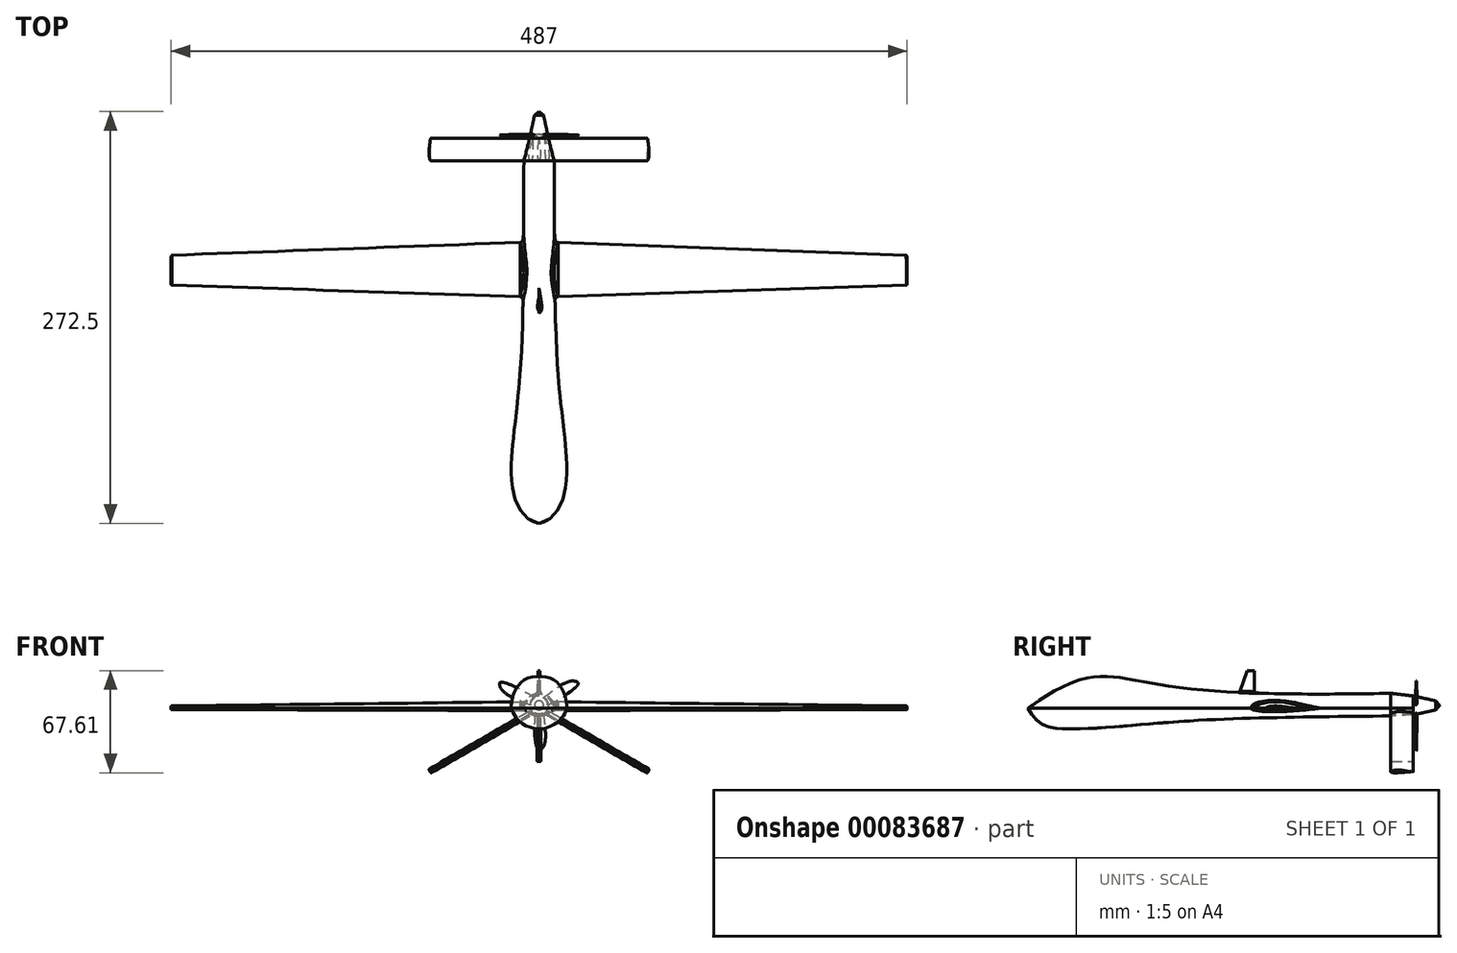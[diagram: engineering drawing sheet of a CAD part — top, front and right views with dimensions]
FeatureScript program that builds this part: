
annotation { "Feature Type Name" : "Feature", "Feature Type Description" : "" }
export const myFeature = defineFeature(function(context is Context, id is Id, definition is map)
    precondition{}
    {
        {
            var Q0;
            Q0=qCreatedBy(makeId("Right.planeOp"),FACE);
            var sketch = newSketch(context, id + "F0", { "sketchPlane" : qUnion([Q0])});
            skLineSegment(sketch, "E0", {"start": v(0, 0) * mm, "end": v(240, 0) * mm});
            skFitSpline(sketch, "E1", {"points": [v(0, 0) * mm, v(37.5, 19.82) * mm, v(94.65, 14.48) * mm, v(240, 10) * mm], "startDerivative": vector(93.49, 65.35) * mm, "endDerivative": vector(326.63, 5.9) * mm});
            skLineSegment(sketch, "E2", {"start": v(240, 10) * mm, "end": v(240, 0) * mm});
            skSolve(sketch);
        }
        {
            var Q0;
            Q0=qCreatedBy(makeId("Front.planeOp"),FACE);
            cPlane(context, id + "F1", {"entities" : qUnion([Q0]), "cplaneType" : CPlaneType.OFFSET, "offset" : 240 * mm, "oppositeDirection" : true, "width" : 150 * mm, "height" : 150 * mm});
        }
        {
            var Q0;
            Q0=qCreatedBy(id+"F1.planeOp",FACE);
            var sketch = newSketch(context, id + "F2", { "sketchPlane" : qUnion([Q0])});
            skArc(sketch, "E3", {"start": v(10, 0) * mm, "mid": v(0, 10) * mm, "end": v(-10, 0) * mm});
            skLineSegment(sketch, "E4", {"start": v(-10, 0) * mm, "end": v(10, 0) * mm});
            skPoint(sketch, "E5.0.start.orphan", {"position": v(0, 10) * mm});
            skSolve(sketch);
        }
        {
            var Q0;
            Q0=qCreatedBy(makeId("Top.planeOp"),FACE);
            var sketch = newSketch(context, id + "F3", { "sketchPlane" : qUnion([Q0])});
            skLineSegment(sketch, "E6", {"start": v(0, 0) * mm, "end": v(0, 272.56) * mm, "construction": true});
            skFitSpline(sketch, "E7.0", {"points": [v(0, 240) * mm, v(-3.33, 240) * mm, v(-6.67, 240) * mm, v(-10, 240) * mm]});
            skFitSpline(sketch, "E8", {"points": [v(-10, 240) * mm, v(-13.37, 88.04) * mm, v(-16.88, 19.92) * mm, v(0, 0) * mm], "startDerivative": vector(-2.86, -342.32) * mm, "endDerivative": vector(133.74, -24.52) * mm});
            skFitSpline(sketch, "E9.MirrorCS", {"points": [v(10, 240) * mm, v(13.37, 88.04) * mm, v(16.88, 19.92) * mm, v(0, 0) * mm], "startDerivative": vector(2.86, -342.32) * mm, "endDerivative": vector(-133.74, -24.52) * mm});
            skSolve(sketch);
        }
        {
            var Q0;
            Q0=qCreatedBy(makeId("Front.planeOp"),FACE);
            cPlane(context, id + "F4", {"entities" : qUnion([Q0]), "cplaneType" : CPlaneType.OFFSET, "offset" : 37.5 * mm, "oppositeDirection" : true, "width" : 150 * mm, "height" : 150 * mm});
        }
        {
            var Q0;
            Q0=qCreatedBy(id+"F4.planeOp",FACE);
            var sketch = newSketch(context, id + "F5", { "sketchPlane" : qUnion([Q0])});
            skArc(sketch, "E10", {"start": v(18.28, 0) * mm, "mid": v(0, 19.82) * mm, "end": v(-18.28, 0) * mm});
            skLineSegment(sketch, "E11", {"start": v(-18.28, 0) * mm, "end": v(18.28, 0) * mm});
            skSolve(sketch);
        }
        {
            var Q0;
            Q0=qCreatedBy(makeId("Front.planeOp"),FACE);
            cPlane(context, id + "F6", {"entities" : qUnion([Q0]), "cplaneType" : CPlaneType.OFFSET, "offset" : 150 * mm, "oppositeDirection" : true, "width" : 150 * mm, "height" : 150 * mm});
        }
        {
            var Q0;
            Q0=qCreatedBy(id+"F6.planeOp",FACE);
            var sketch = newSketch(context, id + "F7", { "sketchPlane" : qUnion([Q0])});
            skArc(sketch, "E12", {"start": v(10.54, 0) * mm, "mid": v(0, 10.12) * mm, "end": v(-10.54, 0) * mm});
            skLineSegment(sketch, "E13", {"start": v(-10.54, 0) * mm, "end": v(10.54, 0) * mm});
            skSolve(sketch);
        }
        {
            var Q0;
            Q0=makeQuery(id+"F2.imprint","IMPRINT",FACE,{"disambiguationData":[TD([[makeQuery(id+"F2.imprint","IMPRINT",EDGE,{"derivedFrom":sQuery(id+"F2.wireOp",EDGE,"E3")}),1.0]])]});
            var Q1;
            Q1=makeQuery(id+"F7.imprint","IMPRINT",FACE,{"disambiguationData":[TD([[makeQuery(id+"F7.imprint","IMPRINT",EDGE,{"derivedFrom":sQuery(id+"F7.wireOp",EDGE,"E12")}),1.0]])]});
            var Q2;
            Q2=makeQuery(id+"F5.imprint","IMPRINT",FACE,{"disambiguationData":[TD([[makeQuery(id+"F5.imprint","IMPRINT",EDGE,{"derivedFrom":sQuery(id+"F5.wireOp",EDGE,"E10")}),1.0]])]});
            var Q3;
            Q3=sQuery(id+"F3.wireOp",VERTEX,"E9.MirrorCS.3.internal");
            var Q4;
            Q4=sQuery(id+"F0.wireOp",EDGE,"E1");
            var Q5;
            Q5=sQuery(id+"F3.wireOp",EDGE,"E9.MirrorCS");
            var Q6;
            Q6=sQuery(id+"F3.wireOp",EDGE,"E8");
            loft(context, id + "F8", {"addGuides" : true, "sheetProfilesArray" : [{ "sheetProfileEntities" : qUnion([Q0]) }, { "sheetProfileEntities" : qUnion([Q1]) }, { "sheetProfileEntities" : qUnion([Q2]) }, { "sheetProfileEntities" : qUnion([Q3]) }], "guidesArray" : [{ "guideEntities" : qUnion([Q4]), "guideDerivativeType" : LoftGuideDerivativeType.DEFAULT, "guideDerivativeMagnitude" : 1 }, { "guideEntities" : qUnion([Q5]), "guideDerivativeType" : LoftGuideDerivativeType.DEFAULT, "guideDerivativeMagnitude" : 1 }, { "guideEntities" : qUnion([Q6]), "guideDerivativeType" : LoftGuideDerivativeType.DEFAULT, "guideDerivativeMagnitude" : 1 }]});
        }
        {
            var Q0;
            Q0=qCreatedBy(makeId("Right.planeOp"),FACE);
            var sketch = newSketch(context, id + "F9", { "sketchPlane" : qUnion([Q0])});
            skPoint(sketch, "E14.0", {"position": v(240, 0) * mm});
            skFitSpline(sketch, "E15", {"points": [v(0, 0) * mm, v(16.5, -12.8) * mm, v(84.8, -9.9) * mm, v(240, -5) * mm], "startDerivative": vector(89.7, -143.98) * mm, "endDerivative": vector(544.57, 5.36) * mm});
            skLineSegment(sketch, "E16", {"start": v(0, 0) * mm, "end": v(240, 0) * mm});
            skSolve(sketch);
        }
        {
            var Q0;
            Q0=qCreatedBy(id+"F1.planeOp",FACE);
            var sketch = newSketch(context, id + "F10", { "sketchPlane" : qUnion([Q0])});
            skFitSpline(sketch, "E17.0", {"points": [v(0, 0) * mm, v(-3.33, 0) * mm, v(-6.67, 0) * mm, v(-10, 0) * mm]});
            skLineSegment(sketch, "E18.0", {"start": v(-10, 0) * mm, "end": v(10, 0) * mm});
            skArc(sketch, "E19", {"start": v(-10, 0) * mm, "mid": v(0, -5) * mm, "end": v(10, 0) * mm});
            skSolve(sketch);
        }
        {
            var Q0;
            Q0=qCreatedBy(id+"F6.planeOp",FACE);
            var sketch = newSketch(context, id + "F11", { "sketchPlane" : qUnion([Q0])});
            skArc(sketch, "E20", {"start": v(-10.54, 0) * mm, "mid": v(0, -6.4) * mm, "end": v(10.54, 0) * mm});
            skLineSegment(sketch, "E21", {"start": v(10.54, 0) * mm, "end": v(-10.54, 0) * mm});
            skSolve(sketch);
        }
        {
            var Q0;
            Q0=qCreatedBy(id+"F4.planeOp",FACE);
            var sketch = newSketch(context, id + "F12", { "sketchPlane" : qUnion([Q0])});
            skArc(sketch, "E22", {"start": v(-18.28, 0) * mm, "mid": v(0, -13.44) * mm, "end": v(18.28, 0) * mm});
            skLineSegment(sketch, "E23", {"start": v(-18.28, 0) * mm, "end": v(18.28, 0) * mm});
            skSolve(sketch);
        }
        {
            var Q1;
            {var subQ0=sQuery(id+"F10.wireOp",EDGE,"E19");Q1=makeQuery(id+"F10.imprint","IMPRINT",FACE,{"disambiguationData":[TD([[makeQuery(id+"F10.imprint","IMPRINT",EDGE,{"derivedFrom":subQ0}),1.0]])]});}
            var Q2;
            Q2=makeQuery(id+"F11.imprint","IMPRINT",FACE,{"disambiguationData":[TD([[makeQuery(id+"F11.imprint","IMPRINT",EDGE,{"derivedFrom":sQuery(id+"F11.wireOp",EDGE,"E20")}),1.0]])]});
            var Q3;
            Q3=makeQuery(id+"F12.imprint","IMPRINT",FACE,{"disambiguationData":[TD([[makeQuery(id+"F12.imprint","IMPRINT",EDGE,{"derivedFrom":sQuery(id+"F12.wireOp",EDGE,"E22")}),1.0]])]});
            var Q4;
            Q4=sQuery(id+"F9.wireOp",VERTEX,"E15.0.internal");
            var Q5;
            Q5=sQuery(id+"F3.wireOp",EDGE,"E8");
            var Q6;
            Q6=sQuery(id+"F3.wireOp",EDGE,"E9.MirrorCS");
            var Q7;
            Q7=sQuery(id+"F9.wireOp",EDGE,"E15");
            loft(context, id + "F13", {"operationType" : NewBodyOperationType.ADD, "addGuides" : true, "sheetProfilesArray" : [{ "sheetProfileEntities" : qUnion([Q1]) }, { "sheetProfileEntities" : qUnion([Q2]) }, { "sheetProfileEntities" : qUnion([Q3]) }, { "sheetProfileEntities" : qUnion([Q4]) }], "guidesArray" : [{ "guideEntities" : qUnion([Q5]), "guideDerivativeType" : LoftGuideDerivativeType.DEFAULT, "guideDerivativeMagnitude" : 1 }, { "guideEntities" : qUnion([Q6]), "guideDerivativeType" : LoftGuideDerivativeType.DEFAULT, "guideDerivativeMagnitude" : 1 }, { "guideEntities" : qUnion([Q7]), "guideDerivativeType" : LoftGuideDerivativeType.DEFAULT, "guideDerivativeMagnitude" : 1 }]});
        }
        {
            var Q0;
            Q0=qCreatedBy(makeId("Right.planeOp"),FACE);
            var sketch = newSketch(context, id + "F14", { "sketchPlane" : qUnion([Q0])});
            skLineSegment(sketch, "E24", {"start": v(0, 0) * mm, "end": v(150, 0) * mm, "construction": true});
            skLineSegment(sketch, "E25", {"start": v(150, 0) * mm, "end": v(186, 0) * mm, "construction": true});
            skFitSpline(sketch, "E26", {"points": [v(150, 0) * mm, v(162.77, 4.35) * mm, v(186, 0) * mm], "startDerivative": vector(1.89, 17.28) * mm, "endDerivative": vector(43.95, -12.7) * mm});
            skFitSpline(sketch, "E27", {"points": [v(150, 0) * mm, v(161.94, -1.41) * mm, v(186, 0) * mm], "startDerivative": vector(11.14, -7.95) * mm, "endDerivative": vector(52.3, 6.57) * mm});
            skSolve(sketch);
        }
        {
            var Q0;
            Q0=qSketchRegion(id+"F14",true);
            extrude(context, id + "F15", {"entities" : qUnion([Q0]), "operationType" : NewBodyOperationType.ADD, "endBound" : BoundingType.SYMMETRIC, "depth" : 25 * mm});
        }
        {
            var Q0;
            Q0=qCreatedBy(makeId("Right.planeOp"),FACE);
            cPlane(context, id + "F16", {"entities" : qUnion([Q0]), "cplaneType" : CPlaneType.OFFSET, "offset" : 243.5 * mm, "width" : 150 * mm, "height" : 150 * mm});
        }
        {
            var Q0;
            Q0=qCreatedBy(id+"F16.planeOp",FACE);
            var sketch = newSketch(context, id + "F17", { "sketchPlane" : qUnion([Q0])});
            skFitSpline(sketch, "E28.0.0", {"points": [v(186, 0) * mm, v(177.65, 2.41) * mm, v(165.41, 6.33) * mm, v(150.27, 2.48) * mm, v(150, 0) * mm]});
            skFitSpline(sketch, "E28.0.1", {"points": [v(150, 0) * mm, v(151.54, -1.1) * mm, v(164.41, -1.68) * mm, v(175.78, -1.28) * mm, v(186, 0) * mm]});
            skLineSegment(sketch, "E29", {"start": v(142.65, 0) * mm, "end": v(197.39, 0) * mm, "construction": true});
            skFitSpline(sketch, "E30", {"points": [v(157.7, 0) * mm, v(162.9, 1.58) * mm, v(177.41, 0) * mm], "startDerivative": vector(0.8, 8.3) * mm, "endDerivative": vector(32.19, -4.29) * mm});
            skFitSpline(sketch, "E31", {"points": [v(157.7, 0) * mm, v(164.23, -0.7) * mm, v(177.41, 0) * mm], "startDerivative": vector(2.27, -4.37) * mm, "endDerivative": vector(24.46, 2.77) * mm});
            skSolve(sketch);
        }
        {
            var Q0;
            Q0=makeQuery(id+"F17.imprint","IMPRINT",FACE,{"disambiguationData":[TD([[makeQuery(id+"F17.imprint","IMPRINT",EDGE,{"derivedFrom":sQuery(id+"F17.wireOp",EDGE,"E30")}),-1.0]])]});
            var Q1;
            Q1=makeQuery(id+"F15.opExtrude","CAP_FACE",FACE,{"disambiguationData":[OSD([sQuery(id+"F14.wireOp",EDGE,"E26"),sQuery(id+"F14.wireOp",EDGE,"E27")])],"isStart":false});
            loft(context, id + "F18", {"sheetProfilesArray" : [{ "sheetProfileEntities" : qUnion([Q0]) }, { "sheetProfileEntities" : qUnion([Q1]) }]});
        }
        {
            var Q0;
            {var subQ0=sQuery(id+"F17.wireOp",EDGE,"E30");var subQ1=sQuery(id+"F17.wireOp",EDGE,"E31");Q0=makeQuery(id+"F18.opLoft","MID_CAP_EDGE",EDGE,{"disambiguationData":[OSD([subQ0,subQ1]),TDD([makeQuery(id+"F17.imprint","INTERSECT",VERTEX,{"disambiguationData":[OD(0.0)],"derivedFrom":[subQ0,subQ1]}),makeQuery(id+"F17.imprint","INTERSECT",VERTEX,{"disambiguationData":[OD(1.0)],"derivedFrom":[subQ0,subQ1]}),makeQuery(id+"F17.imprint","IMPRINT",EDGE,{"derivedFrom":subQ0})])],"capPos":0.0});}
            fillet(context, id + "F19", {"entities" : qUnion([Q0]), "radius" : 0.5 * mm, "tangentPropagation" : true, "allowEdgeOverflow" : false});
        }
        {
            var Q0;
            Q0=makeQuery(id+"F18.opLoft","SWEPT_BODY",BODY,{"disambiguationData":[OSD([sQuery(id+"F14.wireOp",EDGE,"E26"),sQuery(id+"F14.wireOp",EDGE,"E27"),makeQuery(id+"F17.imprint","IMPRINT",FACE,{"disambiguationData":[TD([[makeQuery(id+"F17.imprint","IMPRINT",EDGE,{"derivedFrom":sQuery(id+"F17.wireOp",EDGE,"E30")}),-1.0]])]})])]});
            var Q1;
            Q1=qCreatedBy(makeId("Right.planeOp"),FACE);
            mirror(context, id + "F20", {"operationType" : NewBodyOperationType.ADD, "entities" : qUnion([Q0]), "mirrorPlane" : qUnion([Q1])});
        }
        {
            var Q0;
            Q0=qCreatedBy(makeId("Front.planeOp"),FACE);
            cPlane(context, id + "F21", {"entities" : qUnion([Q0]), "cplaneType" : CPlaneType.OFFSET, "offset" : 255 * mm, "oppositeDirection" : true, "width" : 150 * mm, "height" : 150 * mm});
        }
        {
            var Q0;
            Q0=qCreatedBy(id+"F21.planeOp",FACE);
            var sketch = newSketch(context, id + "F22", { "sketchPlane" : qUnion([Q0])});
            skFitSpline(sketch, "E32.0.0", {"points": [v(0, 10) * mm, v(0.66, 10) * mm, v(1.3, 9.94) * mm, v(1.95, 9.8) * mm, v(2.6, 9.68) * mm, v(3.22, 9.5) * mm, v(3.83, 9.24) * mm, v(4.43, 8.99) * mm, v(5, 8.68) * mm, v(5.56, 8.31) * mm, v(6.1, 7.95) * mm, v(6.6, 7.54) * mm, v(7.07, 7.07) * mm, v(7.53, 6.6) * mm, v(7.95, 6.1) * mm, v(8.31, 5.56) * mm, v(8.68, 5.01) * mm, v(8.99, 4.43) * mm, v(9.24, 3.83) * mm, v(9.49, 3.22) * mm, v(9.68, 2.6) * mm, v(9.8, 1.95) * mm, v(9.94, 1.3) * mm, v(10, 0.66) * mm, v(10, 0) * mm]});
            skFitSpline(sketch, "E32.0.1", {"points": [v(10, 0) * mm, v(9.42, -0.78) * mm, v(8.75, -1.47) * mm, v(8, -2.1) * mm, v(7.27, -2.72) * mm, v(6.46, -3.25) * mm, v(5.6, -3.68) * mm, v(4.72, -4.11) * mm, v(3.82, -4.44) * mm, v(2.87, -4.67) * mm, v(1.93, -4.89) * mm, v(0.97, -5) * mm, v(0, -5) * mm]});
            skFitSpline(sketch, "E32.0.2", {"points": [v(0, -5) * mm, v(-0.97, -5) * mm, v(-1.93, -4.89) * mm, v(-2.87, -4.67) * mm, v(-3.82, -4.44) * mm, v(-4.72, -4.11) * mm, v(-5.6, -3.68) * mm, v(-6.46, -3.25) * mm, v(-7.26, -2.72) * mm, v(-8, -2.1) * mm, v(-8.75, -1.48) * mm, v(-9.42, -0.78) * mm, v(-10, 0) * mm]});
            skFitSpline(sketch, "E32.0.3", {"points": [v(-10, 0) * mm, v(-10, 0.66) * mm, v(-9.94, 1.3) * mm, v(-9.8, 1.95) * mm, v(-9.68, 2.6) * mm, v(-9.5, 3.22) * mm, v(-9.24, 3.83) * mm, v(-8.99, 4.43) * mm, v(-8.68, 5) * mm, v(-8.31, 5.56) * mm, v(-7.95, 6.1) * mm, v(-7.54, 6.6) * mm, v(-7.07, 7.07) * mm, v(-6.6, 7.53) * mm, v(-6.1, 7.95) * mm, v(-5.56, 8.31) * mm, v(-5.01, 8.68) * mm, v(-4.43, 8.99) * mm, v(-3.83, 9.24) * mm, v(-3.22, 9.49) * mm, v(-2.6, 9.68) * mm, v(-1.95, 9.8) * mm, v(-1.3, 9.94) * mm, v(-0.66, 10) * mm, v(0, 10) * mm]});
            skCircle(sketch, "E33", {"center": v(0, 2) * mm, "radius": 6.25 * mm});
            skLineSegment(sketch, "E34", {"start": v(10, 0) * mm, "end": v(-10, 0) * mm, "construction": true});
            skPoint(sketch, "E35", {"position": v(5.92, 0) * mm});
            skPoint(sketch, "E36", {"position": v(-5.92, 0) * mm});
            skPoint(sketch, "E37", {"position": v(0, 8.25) * mm});
            skPoint(sketch, "E38", {"position": v(0, -4.25) * mm});
            skSolve(sketch);
        }
        {
            var Q0;
            Q0=qCreatedBy(makeId("Front.planeOp"),FACE);
            cPlane(context, id + "F23", {"entities" : qUnion([Q0]), "cplaneType" : CPlaneType.OFFSET, "offset" : 270 * mm, "oppositeDirection" : true, "width" : 150 * mm, "height" : 150 * mm});
        }
        {
            var Q0;
            Q0=qCreatedBy(makeId("Top.planeOp"),FACE);
            var sketch = newSketch(context, id + "F24", { "sketchPlane" : qUnion([Q0])});
            skPoint(sketch, "E39.0", {"position": v(-10, 240) * mm});
            skPoint(sketch, "E40.0", {"position": v(10, 240) * mm});
            skPoint(sketch, "E41.0", {"position": v(-5.92, 255) * mm});
            skPoint(sketch, "E42.0", {"position": v(5.92, 255) * mm});
            skLineSegment(sketch, "E43", {"start": v(10, 240) * mm, "end": v(5.92, 255) * mm});
            skLineSegment(sketch, "E44", {"start": v(-10, 240) * mm, "end": v(-5.92, 255) * mm});
            skSolve(sketch);
        }
        {
            var Q1;
            {var subQ0=sQuery(id+"F10.wireOp",EDGE,"E19");Q1=makeQuery(id+"F13.boolean.opBoolean","MERGE",FACE,{"derivedFrom":[makeQuery(id+"F8.opLoft","CAP_FACE",FACE,{"disambiguationData":[OSD([makeQuery(id+"F2.imprint","IMPRINT",FACE,{"disambiguationData":[TD([[makeQuery(id+"F2.imprint","IMPRINT",EDGE,{"derivedFrom":sQuery(id+"F2.wireOp",EDGE,"E3")}),1.0]])]})])],"isStart":true}),makeQuery(id+"F13.opLoft","CAP_FACE",FACE,{"disambiguationData":[OSD([makeQuery(id+"F10.imprint","IMPRINT",FACE,{"disambiguationData":[TD([[makeQuery(id+"F10.imprint","IMPRINT",EDGE,{"derivedFrom":subQ0}),1.0]])]})])],"isStart":true})]});}
            var Q2;
            Q2=makeQuery(id+"F22.imprint","IMPRINT",FACE,{"disambiguationData":[TD([[makeQuery(id+"F22.imprint","IMPRINT",EDGE,{"derivedFrom":sQuery(id+"F22.wireOp",EDGE,"E33")}),1.0]])]});
            var Q3;
            Q3=sQuery(id+"F24.wireOp",EDGE,"E44");
            var Q4;
            Q4=sQuery(id+"F24.wireOp",EDGE,"E43");
            loft(context, id + "F25", {"operationType" : NewBodyOperationType.ADD, "addGuides" : true, "sheetProfilesArray" : [{ "sheetProfileEntities" : qUnion([Q1]) }, { "sheetProfileEntities" : qUnion([Q2]) }], "guidesArray" : [{ "guideEntities" : qUnion([Q3]), "guideDerivativeType" : LoftGuideDerivativeType.DEFAULT, "guideDerivativeMagnitude" : 1 }, { "guideEntities" : qUnion([Q4]), "guideDerivativeType" : LoftGuideDerivativeType.DEFAULT, "guideDerivativeMagnitude" : 1 }]});
        }
        {
            var Q0;
            Q0=qCreatedBy(id+"F23.planeOp",FACE);
            var sketch = newSketch(context, id + "F26", { "sketchPlane" : qUnion([Q0])});
            skCircle(sketch, "E45", {"center": v(0, 2) * mm, "radius": 3 * mm});
            skSolve(sketch);
        }
        {
            var Q1;
            Q1=makeQuery(id+"F25.opLoft","CAP_FACE",FACE,{"disambiguationData":[OSD([makeQuery(id+"F22.imprint","IMPRINT",FACE,{"disambiguationData":[TD([[makeQuery(id+"F22.imprint","IMPRINT",EDGE,{"derivedFrom":sQuery(id+"F22.wireOp",EDGE,"E33")}),1.0]])]})])],"isStart":true});
            var Q2;
            Q2=makeQuery(id+"F26.imprint","IMPRINT",FACE,{"disambiguationData":[TD([[makeQuery(id+"F26.imprint","IMPRINT",EDGE,{"derivedFrom":sQuery(id+"F26.wireOp",EDGE,"E45")}),1.0]])]});
            loft(context, id + "F27", {"operationType" : NewBodyOperationType.ADD, "sheetProfilesArray" : [{ "sheetProfileEntities" : qUnion([Q1]) }, { "sheetProfileEntities" : qUnion([Q2]) }]});
        }
        {
            var Q0;
            Q0=qCreatedBy(makeId("Front.planeOp"),FACE);
            cPlane(context, id + "F28", {"entities" : qUnion([Q0]), "cplaneType" : CPlaneType.OFFSET, "offset" : 272.5 * mm, "oppositeDirection" : true, "width" : 150 * mm, "height" : 150 * mm});
        }
        {
            var Q0;
            Q0=qCreatedBy(id+"F28.planeOp",FACE);
            var sketch = newSketch(context, id + "F29", { "sketchPlane" : qUnion([Q0])});
            skFitSpline(sketch, "E46.0.0", {"points": [v(3, 2) * mm, v(3, 1.6) * mm, v(2.92, 1.22) * mm, v(2.77, 0.85) * mm, v(2.62, 0.49) * mm, v(2.4, 0.16) * mm, v(2.12, -0.12) * mm, v(1.84, -0.4) * mm, v(1.52, -0.62) * mm, v(1.15, -0.77) * mm, v(0.78, -0.92) * mm, v(0.4, -1) * mm, v(0, -1) * mm]});
            skFitSpline(sketch, "E46.0.1", {"points": [v(0, -1) * mm, v(-0.4, -1) * mm, v(-0.78, -0.92) * mm, v(-1.15, -0.77) * mm, v(-1.51, -0.62) * mm, v(-1.84, -0.4) * mm, v(-2.12, -0.12) * mm, v(-2.4, 0.16) * mm, v(-2.62, 0.48) * mm, v(-2.77, 0.85) * mm, v(-2.92, 1.22) * mm, v(-3, 1.6) * mm, v(-3, 2) * mm]});
            skFitSpline(sketch, "E46.0.2", {"points": [v(-3, 2) * mm, v(-3, 2.4) * mm, v(-2.92, 2.78) * mm, v(-2.77, 3.15) * mm, v(-2.62, 3.51) * mm, v(-2.4, 3.84) * mm, v(-2.12, 4.12) * mm, v(-1.84, 4.4) * mm, v(-1.52, 4.62) * mm, v(-1.15, 4.77) * mm, v(-0.78, 4.92) * mm, v(-0.4, 5) * mm, v(0, 5) * mm]});
            skFitSpline(sketch, "E46.0.3", {"points": [v(0, 5) * mm, v(0.4, 5) * mm, v(0.78, 4.92) * mm, v(1.15, 4.77) * mm, v(1.51, 4.62) * mm, v(1.84, 4.4) * mm, v(2.12, 4.12) * mm, v(2.4, 3.84) * mm, v(2.62, 3.52) * mm, v(2.77, 3.15) * mm, v(2.92, 2.78) * mm, v(3, 2.4) * mm, v(3, 2) * mm]});
            skPoint(sketch, "E47", {"position": v(0, 2) * mm});
            skSolve(sketch);
        }
        {
            var Q1;
            Q1=makeQuery(id+"F27.opLoft","CAP_FACE",FACE,{"disambiguationData":[OSD([makeQuery(id+"F26.imprint","IMPRINT",FACE,{"disambiguationData":[TD([[makeQuery(id+"F26.imprint","IMPRINT",EDGE,{"derivedFrom":sQuery(id+"F26.wireOp",EDGE,"E45")}),1.0]])]})])],"isStart":true});
            var Q2;
            Q2=sQuery(id+"F29.wireOp",VERTEX,"E47");
            loft(context, id + "F30", {"operationType" : NewBodyOperationType.ADD, "sheetProfilesArray" : [{ "sheetProfileEntities" : qUnion([Q1]) }, { "sheetProfileEntities" : qUnion([Q2]) }]});
        }
        {
            var Q0;
            Q0=qCreatedBy(makeId("Right.planeOp"),FACE);
            cPlane(context, id + "F31", {"entities" : qUnion([Q0]), "cplaneType" : CPlaneType.OFFSET, "offset" : 72 * mm, "width" : 150 * mm, "height" : 150 * mm});
        }
        {
            var Q0;
            Q0=qCreatedBy(id+"F31.planeOp",FACE);
            var sketch = newSketch(context, id + "F32", { "sketchPlane" : qUnion([Q0])});
            skLineSegment(sketch, "E48", {"start": v(0, 0) * mm, "end": v(0, -42) * mm, "construction": true});
            skLineSegment(sketch, "E49", {"start": v(0, -42) * mm, "end": v(271.23, -42) * mm});
            skSolve(sketch);
        }
        {
            assignVariable(context, id + "F33", {"name" : "angle", "anyValue" : 120});
        }
        {
            var Q0;
            Q0=sQuery(id+"F32.wireOp",EDGE,"E49");
            cPlane(context, id + "F34", {"entities" : qUnion([Q0]), "cplaneType" : CPlaneType.LINE_ANGLE, "offset" : 150 * mm, "angle" : (getVariable(context, 'angle')) * degree, "width" : 150 * mm, "height" : 150 * mm});
        }
        {
            var Q0;
            Q0=qCreatedBy(id+"F34.planeOp",FACE);
            var sketch = newSketch(context, id + "F35", { "sketchPlane" : qUnion([Q0])});
            skFitSpline(sketch, "E50.0", {"points": [v(240, 5) * mm, v(245, 4.32) * mm, v(250, 3.64) * mm, v(255, 2.96) * mm], "construction": true});
            skLineSegment(sketch, "E51.0", {"start": v(0, -0.37) * mm, "end": v(242.6, -0.37) * mm, "construction": true});
            skPoint(sketch, "E52.orphan", {"position": v(271.23, -0.37) * mm});
            skFitSpline(sketch, "E53", {"points": [v(240, -0.37) * mm, v(244.56, 1.55) * mm, v(255, -0.37) * mm], "startDerivative": vector(6.04, 10.7) * mm, "endDerivative": vector(29.02, -7.53) * mm});
            skFitSpline(sketch, "E54", {"points": [v(240, -0.37) * mm, v(244.42, -1.27) * mm, v(255, -0.37) * mm], "startDerivative": vector(3.63, -7.22) * mm, "endDerivative": vector(30.34, 2.29) * mm});
            skSolve(sketch);
        }
        {
            var Q0;
            Q0=makeQuery(id+"F35.imprint","IMPRINT",FACE,{"disambiguationData":[TD([[makeQuery(id+"F35.imprint","IMPRINT",EDGE,{"derivedFrom":sQuery(id+"F35.wireOp",EDGE,"E53")}),-1.0]])]});
            extrude(context, id + "F36", {"entities" : qUnion([Q0]), "oppositeDirection" : true, "depth" : 80 * mm});
        }
        {
            var Q0;
            Q0=makeQuery(id+"F36.opExtrude","CAP_EDGE",EDGE,{"disambiguationData":[OSD([sQuery(id+"F35.wireOp",EDGE,"E53")])],"isStart":true});
            var Q1;
            Q1=makeQuery(id+"F36.opExtrude","CAP_EDGE",EDGE,{"disambiguationData":[OSD([sQuery(id+"F35.wireOp",EDGE,"E54")])],"isStart":true});
            fillet(context, id + "F37", {"entities" : qUnion([Q0, Q1]), "radius" : 0.5 * mm, "tangentPropagation" : true, "allowEdgeOverflow" : false});
        }
        {
            var Q0;
            Q0=makeQuery(id+"F36.opExtrude","SWEPT_BODY",BODY,{"disambiguationData":[OSD([sQuery(id+"F35.wireOp",EDGE,"E53"),sQuery(id+"F35.wireOp",EDGE,"E54")])]});
            var Q1;
            Q1=qCreatedBy(makeId("Right.planeOp"),FACE);
            mirror(context, id + "F38", {"operationType" : NewBodyOperationType.ADD, "entities" : qUnion([Q0]), "mirrorPlane" : qUnion([Q1])});
        }
        {
            var Q0;
            Q0=qCreatedBy(makeId("Top.planeOp"),FACE);
            var sketch = newSketch(context, id + "F39", { "sketchPlane" : qUnion([Q0])});
            skLineSegment(sketch, "E55", {"start": v(0, 0) * mm, "end": v(0, 257) * mm, "construction": true});
            skEllipse(sketch, "E56", {"center": v(0, 257) * mm, "majorRadius": 2.5 * mm, "minorRadius": 0.6 * mm, "majorAxis": v(-1, 0)});
            skSolve(sketch);
        }
        {
            var Q0;
            Q0=qCreatedBy(makeId("Front.planeOp"),FACE);
            cPlane(context, id + "F40", {"entities" : qUnion([Q0]), "cplaneType" : CPlaneType.OFFSET, "offset" : 257 * mm, "oppositeDirection" : true, "width" : 150 * mm, "height" : 150 * mm});
        }
        {
            var Q0;
            Q0=qCreatedBy(id+"F40.planeOp",FACE);
            var sketch = newSketch(context, id + "F41", { "sketchPlane" : qUnion([Q0])});
            skLineSegment(sketch, "E57.0", {"start": v(2.5, 0) * mm, "end": v(-2.5, 0) * mm});
            skLineSegment(sketch, "E58", {"start": v(0, 0) * mm, "end": v(0, -28) * mm, "construction": true});
            skFitSpline(sketch, "E59", {"points": [v(2.5, 0) * mm, v(4.19, -20.46) * mm, v(0, -28) * mm], "startDerivative": vector(5.82, -52.04) * mm, "endDerivative": vector(-22.98, -9.89) * mm});
            skFitSpline(sketch, "E60", {"points": [v(-2.5, 0) * mm, v(-2.5, -20.53) * mm, v(0, -28) * mm], "startDerivative": vector(-3.63, -41.05) * mm, "endDerivative": vector(9.75, -1.43) * mm});
            skSolve(sketch);
        }
        {
            var Q1;
            Q1=makeQuery(id+"F39.imprint","IMPRINT",FACE,{"disambiguationData":[TD([[makeQuery(id+"F39.imprint","IMPRINT",EDGE,{"derivedFrom":sQuery(id+"F39.wireOp",EDGE,"E56")}),1.0]])]});
            var Q2;
            Q2=sQuery(id+"F41.wireOp",VERTEX,"E60.end");
            var Q3;
            Q3=sQuery(id+"F41.wireOp",EDGE,"E59");
            var Q4;
            Q4=sQuery(id+"F41.wireOp",EDGE,"E60");
            loft(context, id + "F42", {"addGuides" : true, "sheetProfilesArray" : [{ "sheetProfileEntities" : qUnion([Q1]) }, { "sheetProfileEntities" : qUnion([Q2]) }], "guidesArray" : [{ "guideEntities" : qUnion([Q3]), "guideDerivativeType" : LoftGuideDerivativeType.DEFAULT, "guideDerivativeMagnitude" : 1 }, { "guideEntities" : qUnion([Q4]), "guideDerivativeType" : LoftGuideDerivativeType.DEFAULT, "guideDerivativeMagnitude" : 1 }]});
        }
        {
            var Q0;
            Q0=qCreatedBy(makeId("Top.planeOp"),FACE);
            cPlane(context, id + "F43", {"entities" : qUnion([Q0]), "cplaneType" : CPlaneType.OFFSET, "offset" : 2 * mm, "width" : 150 * mm, "height" : 150 * mm});
        }
        {
            var Q0;
            Q0=qCreatedBy(id+"F43.planeOp",FACE);
            var sketch = newSketch(context, id + "F44", { "sketchPlane" : qUnion([Q0])});
            skLineSegment(sketch, "E61", {"start": v(0, 0) * mm, "end": v(0, 416.26) * mm, "construction": true});
            skSolve(sketch);
        }
        {
            var Q0;
            Q0=makeQuery(id+"F42.opLoft","SWEPT_BODY",BODY,{"disambiguationData":[OSD([makeQuery(id+"F39.imprint","IMPRINT",FACE,{"disambiguationData":[TD([[makeQuery(id+"F39.imprint","IMPRINT",EDGE,{"derivedFrom":sQuery(id+"F39.wireOp",EDGE,"E56")}),1.0]])]}),sQuery(id+"F41.wireOp",VERTEX,"E60.end"),sQuery(id+"F41.wireOp",EDGE,"E59"),sQuery(id+"F41.wireOp",EDGE,"E60")])]});
            var Q1;
            Q1=sQuery(id+"F44.wireOp",EDGE,"E61");
            circularPattern(context, id + "F45", {"operationType" : NewBodyOperationType.ADD, "entities" : qUnion([Q0]), "axis" : qUnion([Q1]), "angle" : 120 * degree, "instanceCount" : 3});
        }
        {
            var Q0;
            Q0=makeQuery(id+"F15.boolean.opBoolean","INTERSECT",EDGE,{"disambiguationData":[OD(1.0)],"derivedFrom":[makeQuery(id+"F13.opLoft","SWEPT_FACE",FACE,{"disambiguationData":[OSD([sQuery(id+"F3.wireOp",EDGE,"E8"),sQuery(id+"F9.wireOp",EDGE,"E15"),sQuery(id+"F10.wireOp",EDGE,"E19"),sQuery(id+"F11.wireOp",EDGE,"E20"),sQuery(id+"F12.wireOp",EDGE,"E22")])]}),makeQuery(id+"F15.opExtrude","SWEPT_FACE",FACE,{"disambiguationData":[OSD([sQuery(id+"F14.wireOp",EDGE,"E27")])]})]});
            var Q1;
            Q1=makeQuery(id+"F15.boolean.opBoolean","INTERSECT",EDGE,{"disambiguationData":[OD(0.0)],"derivedFrom":[makeQuery(id+"F13.opLoft","SWEPT_FACE",FACE,{"disambiguationData":[OSD([sQuery(id+"F3.wireOp",EDGE,"E8"),sQuery(id+"F9.wireOp",EDGE,"E15"),sQuery(id+"F10.wireOp",EDGE,"E19"),sQuery(id+"F11.wireOp",EDGE,"E20"),sQuery(id+"F12.wireOp",EDGE,"E22")])]}),makeQuery(id+"F15.opExtrude","SWEPT_FACE",FACE,{"disambiguationData":[OSD([sQuery(id+"F14.wireOp",EDGE,"E27")])]})]});
            var Q2;
            Q2=makeQuery(id+"F15.boolean.opBoolean","INTERSECT",EDGE,{"disambiguationData":[OD(1.0)],"derivedFrom":[makeQuery(id+"F8.opLoft","SWEPT_FACE",FACE,{"disambiguationData":[OSD([sQuery(id+"F0.wireOp",EDGE,"E1"),sQuery(id+"F2.wireOp",EDGE,"E3"),sQuery(id+"F3.wireOp",EDGE,"E9.MirrorCS"),sQuery(id+"F5.wireOp",EDGE,"E10"),sQuery(id+"F7.wireOp",EDGE,"E12")])]}),makeQuery(id+"F15.opExtrude","SWEPT_FACE",FACE,{"disambiguationData":[OSD([sQuery(id+"F14.wireOp",EDGE,"E26")])]})]});
            var Q3;
            Q3=makeQuery(id+"F15.boolean.opBoolean","INTERSECT",EDGE,{"disambiguationData":[OD(0.0)],"derivedFrom":[makeQuery(id+"F8.opLoft","SWEPT_FACE",FACE,{"disambiguationData":[OSD([sQuery(id+"F0.wireOp",EDGE,"E1"),sQuery(id+"F2.wireOp",EDGE,"E3"),sQuery(id+"F3.wireOp",EDGE,"E9.MirrorCS"),sQuery(id+"F5.wireOp",EDGE,"E10"),sQuery(id+"F7.wireOp",EDGE,"E12")])]}),makeQuery(id+"F15.opExtrude","SWEPT_FACE",FACE,{"disambiguationData":[OSD([sQuery(id+"F14.wireOp",EDGE,"E26")])]})]});
            fillet(context, id + "F46", {"entities" : qUnion([Q0, Q1, Q2, Q3]), "radius" : 2.5 * mm, "tangentPropagation" : true, "allowEdgeOverflow" : false});
        }
        {
            var Q0;
            Q0=qCreatedBy(makeId("Top.planeOp"),FACE);
            cPlane(context, id + "F47", {"entities" : qUnion([Q0]), "cplaneType" : CPlaneType.OFFSET, "offset" : 35 * mm, "oppositeDirection" : true, "width" : 150 * mm, "height" : 150 * mm});
        }
        {
            var Q0;
            Q0=qCreatedBy(id+"F47.planeOp",FACE);
            var sketch = newSketch(context, id + "F48", { "sketchPlane" : qUnion([Q0])});
            skLineSegment(sketch, "E62", {"start": v(0, 0) * mm, "end": v(0, 240) * mm, "construction": true});
            skFitSpline(sketch, "E63", {"points": [v(0, 240) * mm, v(-1.2, 243.6) * mm, v(0, 255) * mm], "startDerivative": vector(-6.2, 2.4) * mm, "endDerivative": vector(4.32, 22.5) * mm});
            skFitSpline(sketch, "E64.MirrorCS", {"points": [v(0, 240) * mm, v(1.2, 243.6) * mm, v(0, 255) * mm], "startDerivative": vector(6.2, 2.4) * mm, "endDerivative": vector(-4.32, 22.5) * mm});
            skSolve(sketch);
        }
        {
            var Q0;
            Q0=makeQuery(id+"F48.imprint","IMPRINT",FACE,{"disambiguationData":[TD([[makeQuery(id+"F48.imprint","IMPRINT",EDGE,{"derivedFrom":sQuery(id+"F48.wireOp",EDGE,"E63")}),-1.0]])]});
            var Q1;
            {var subQ0=makeQuery(id+"F36.opExtrude","SWEPT_FACE",FACE,{"disambiguationData":[OSD([sQuery(id+"F35.wireOp",EDGE,"E53")])]});var subQ1=sQuery(id+"F24.wireOp",EDGE,"E43");var subQ2=sQuery(id+"F22.wireOp",EDGE,"E33");var subQ3=sQuery(id+"F10.wireOp",EDGE,"E19");var subQ4=sQuery(id+"F9.wireOp",EDGE,"E15");var subQ5=makeQuery(id+"F25.opLoft","SWEPT_FACE",FACE,{"disambiguationData":[OSD([sQuery(id+"F3.wireOp",EDGE,"E9.MirrorCS"),subQ4,subQ3,subQ2,subQ1])]});var subQ6=makeQuery(id+"F36.opExtrude","SWEPT_FACE",FACE,{"disambiguationData":[OSD([sQuery(id+"F35.wireOp",EDGE,"E54")])]});Q1=makeQuery(id+"F38.boolean.opBoolean","SPLIT",FACE,{"disambiguationData":[TD([makeQuery(id+"F13.opLoft","SWEPT_FACE",FACE,{"disambiguationData":[OSD([sQuery(id+"F3.wireOp",EDGE,"E8"),subQ4,subQ3,sQuery(id+"F11.wireOp",EDGE,"E20"),sQuery(id+"F12.wireOp",EDGE,"E22")])]}),subQ5,makeQuery(id+"F27.opLoft","SWEPT_FACE",FACE,{"disambiguationData":[OSD([subQ2,subQ1,sQuery(id+"F24.wireOp",EDGE,"E44"),sQuery(id+"F26.wireOp",EDGE,"E45")])]}),subQ0,subQ6,makeQuery(id+"F38.opPattern","COPY",FACE,{"derivedFrom":subQ0,"instanceName":"1"}),makeQuery(id+"F38.opPattern","COPY",FACE,{"derivedFrom":subQ6,"instanceName":"1"})])],"derivedFrom":subQ5});}
            extrude(context, id + "F49", {"entities" : qUnion([Q0]), "operationType" : NewBodyOperationType.ADD, "endBound" : BoundingType.UP_TO_SURFACE, "endBoundEntityFace" : qUnion([Q1]), "depth" : 25 * mm});
        }
        {
            var Q0;
            Q0=qCreatedBy(makeId("Top.planeOp"),FACE);
            cPlane(context, id + "F50", {"entities" : qUnion([Q0]), "cplaneType" : CPlaneType.OFFSET, "offset" : 25 * mm, "width" : 150 * mm, "height" : 150 * mm});
        }
        {
            var Q0;
            Q0=qCreatedBy(id+"F50.planeOp",FACE);
            var sketch = newSketch(context, id + "F51", { "sketchPlane" : qUnion([Q0])});
            skLineSegment(sketch, "E65", {"start": v(0, 0) * mm, "end": v(0, 145) * mm, "construction": true});
            skFitSpline(sketch, "E66", {"points": [v(0, 145) * mm, v(-0.66, 146.79) * mm, v(0, 150) * mm], "startDerivative": vector(-4.26, 2.06) * mm, "endDerivative": vector(2.38, 11.26) * mm});
            skFitSpline(sketch, "E67.MirrorCS", {"points": [v(0, 145) * mm, v(0.66, 146.79) * mm, v(0, 150) * mm], "startDerivative": vector(4.26, 2.06) * mm, "endDerivative": vector(-2.38, 11.26) * mm});
            skSolve(sketch);
        }
        {
            var Q0;
            Q0=qCreatedBy(makeId("Top.planeOp"),FACE);
            cPlane(context, id + "F52", {"entities" : qUnion([Q0]), "cplaneType" : CPlaneType.OFFSET, "offset" : 10 * mm, "width" : 150 * mm, "height" : 150 * mm});
        }
        {
            var Q0;
            Q0=qCreatedBy(id+"F52.planeOp",FACE);
            var sketch = newSketch(context, id + "F53", { "sketchPlane" : qUnion([Q0])});
            skLineSegment(sketch, "E68", {"start": v(0, 0) * mm, "end": v(0, 140) * mm, "construction": true});
            skPoint(sketch, "E69.0", {"position": v(0, 150) * mm});
            skFitSpline(sketch, "E70", {"points": [v(0, 140) * mm, v(-0.92, 142) * mm, v(0, 150) * mm], "startDerivative": vector(-6.44, 5.81) * mm, "endDerivative": vector(4.8, 27.45) * mm});
            skFitSpline(sketch, "E71.MirrorCS", {"points": [v(0, 140) * mm, v(0.92, 142) * mm, v(0, 150) * mm], "startDerivative": vector(6.44, 5.81) * mm, "endDerivative": vector(-4.8, 27.45) * mm});
            skSolve(sketch);
        }
        {
            var Q1;
            Q1=makeQuery(id+"F51.imprint","IMPRINT",FACE,{"disambiguationData":[TD([[makeQuery(id+"F51.imprint","IMPRINT",EDGE,{"derivedFrom":sQuery(id+"F51.wireOp",EDGE,"E66")}),-1.0]])]});
            var Q2;
            Q2=qSketchRegion(id+"F53",true);
            loft(context, id + "F54", {"operationType" : NewBodyOperationType.ADD, "sheetProfilesArray" : [{ "sheetProfileEntities" : qUnion([Q1]) }, { "sheetProfileEntities" : qUnion([Q2]) }]});
        }
        {
            var Q0;
            {var subQ0=sQuery(id+"F53.wireOp",EDGE,"E71.MirrorCS");var subQ1=sQuery(id+"F53.wireOp",EDGE,"E70");var subQ2=sQuery(id+"F51.wireOp",EDGE,"E67.MirrorCS");var subQ3=sQuery(id+"F51.wireOp",EDGE,"E66");Q0=makeQuery(id+"F54.boolean.opBoolean","INTERSECT",EDGE,{"derivedFrom":[makeQuery(id+"F8.opLoft","SWEPT_FACE",FACE,{"disambiguationData":[OSD([sQuery(id+"F0.wireOp",EDGE,"E1"),sQuery(id+"F2.wireOp",EDGE,"E3"),sQuery(id+"F3.wireOp",EDGE,"E9.MirrorCS"),sQuery(id+"F5.wireOp",EDGE,"E10"),sQuery(id+"F7.wireOp",EDGE,"E12")])]}),makeQuery(id+"F54.opLoft","SWEPT_FACE",FACE,{"disambiguationData":[OSD([subQ3,subQ2,subQ1,subQ0]),TDD([makeQuery(id+"F51.imprint","INTERSECT",VERTEX,{"disambiguationData":[OD(0.0)],"derivedFrom":[subQ3,subQ2]}),makeQuery(id+"F51.imprint","INTERSECT",VERTEX,{"disambiguationData":[OD(1.0)],"derivedFrom":[subQ3,subQ2]}),makeQuery(id+"F51.imprint","IMPRINT",EDGE,{"derivedFrom":subQ2}),makeQuery(id+"F53.imprint","INTERSECT",VERTEX,{"disambiguationData":[OD(0.0)],"derivedFrom":[subQ1,subQ0]}),makeQuery(id+"F53.imprint","INTERSECT",VERTEX,{"disambiguationData":[OD(1.0)],"derivedFrom":[subQ1,subQ0]}),makeQuery(id+"F53.imprint","IMPRINT",EDGE,{"derivedFrom":subQ0})])]})]});}
            var Q1;
            {var subQ0=sQuery(id+"F53.wireOp",EDGE,"E70");var subQ1=sQuery(id+"F53.wireOp",EDGE,"E71.MirrorCS");var subQ2=sQuery(id+"F51.wireOp",EDGE,"E66");var subQ3=sQuery(id+"F51.wireOp",EDGE,"E67.MirrorCS");Q1=makeQuery(id+"F54.boolean.opBoolean","INTERSECT",EDGE,{"derivedFrom":[makeQuery(id+"F8.opLoft","SWEPT_FACE",FACE,{"disambiguationData":[OSD([sQuery(id+"F0.wireOp",EDGE,"E1"),sQuery(id+"F2.wireOp",EDGE,"E3"),sQuery(id+"F3.wireOp",EDGE,"E9.MirrorCS"),sQuery(id+"F5.wireOp",EDGE,"E10"),sQuery(id+"F7.wireOp",EDGE,"E12")])]}),makeQuery(id+"F54.opLoft","SWEPT_FACE",FACE,{"disambiguationData":[OSD([subQ2,subQ3,subQ0,subQ1]),TDD([makeQuery(id+"F51.imprint","INTERSECT",VERTEX,{"disambiguationData":[OD(0.0)],"derivedFrom":[subQ2,subQ3]}),makeQuery(id+"F51.imprint","INTERSECT",VERTEX,{"disambiguationData":[OD(1.0)],"derivedFrom":[subQ2,subQ3]}),makeQuery(id+"F51.imprint","IMPRINT",EDGE,{"derivedFrom":subQ2}),makeQuery(id+"F53.imprint","INTERSECT",VERTEX,{"disambiguationData":[OD(0.0)],"derivedFrom":[subQ0,subQ1]}),makeQuery(id+"F53.imprint","INTERSECT",VERTEX,{"disambiguationData":[OD(1.0)],"derivedFrom":[subQ0,subQ1]}),makeQuery(id+"F53.imprint","IMPRINT",EDGE,{"derivedFrom":subQ0})])]})]});}
            fillet(context, id + "F55", {"entities" : qUnion([Q0, Q1]), "radius" : 1 * mm, "tangentPropagation" : true, "allowEdgeOverflow" : false});
        }
    });
